# Revit family: Keilhauer-Toob-Stool+
name_source: partatom
category: Furniture
units: mm (PartAtom-declared; Revit-internal decimal feet)

## family parameters
Always vertical = Yes
Cut with Voids When Loaded = No
OmniClass Number = 23.40.20.00
OmniClass Title = General Furniture and Specialties
Room Calculation Point = No
Shared = No
Work Plane-Based = No

## types (2) — shared parameters
Assembly Code = E2020200
Default Elevation = 0"
Depth = 31 1/2"
Front-Bar-Dist = -1 7/8"
Height = 16 3/4"
Keynote = 12500
Manufacturer = Keilhauer
Product Documentation Link = https://keilhauer.com
Rear-Top-Mid-Dist = 8 13/16"
Revit File Built By = https://servex-us.com
Sustainability = https://keilhauer.com
Type Comments = Toob
URL = https://keilhauer.com
Width = 31 1/2"

## per-type parameters (varying)
| type | Back Bar Dist | Description | Front-Btm-Center-Dist | Front-Btm-Mid-Dist | Rear-Btm-Center-Dist | Rear-Btm-Mid-Dist | Rear-Top-Center-Dist | Seat Height |
| 98110 | -3 11/16" | Counter Stool | 8 3/8" | 9" | 8 5/16" | 11 7/16" | 6 13/32" | 24 1/4" |
| 98120 | -3 5/8" | Bar Stool | 8 11/16" | 9 3/8" | 8 3/4" | 12" | 6 1/2" | 30" |

note: column(s) folded — value = type name in every type: Model

## geometry (parser evidence)
native form markers: Sweep x4
no freeform markers — native parametric forms only
